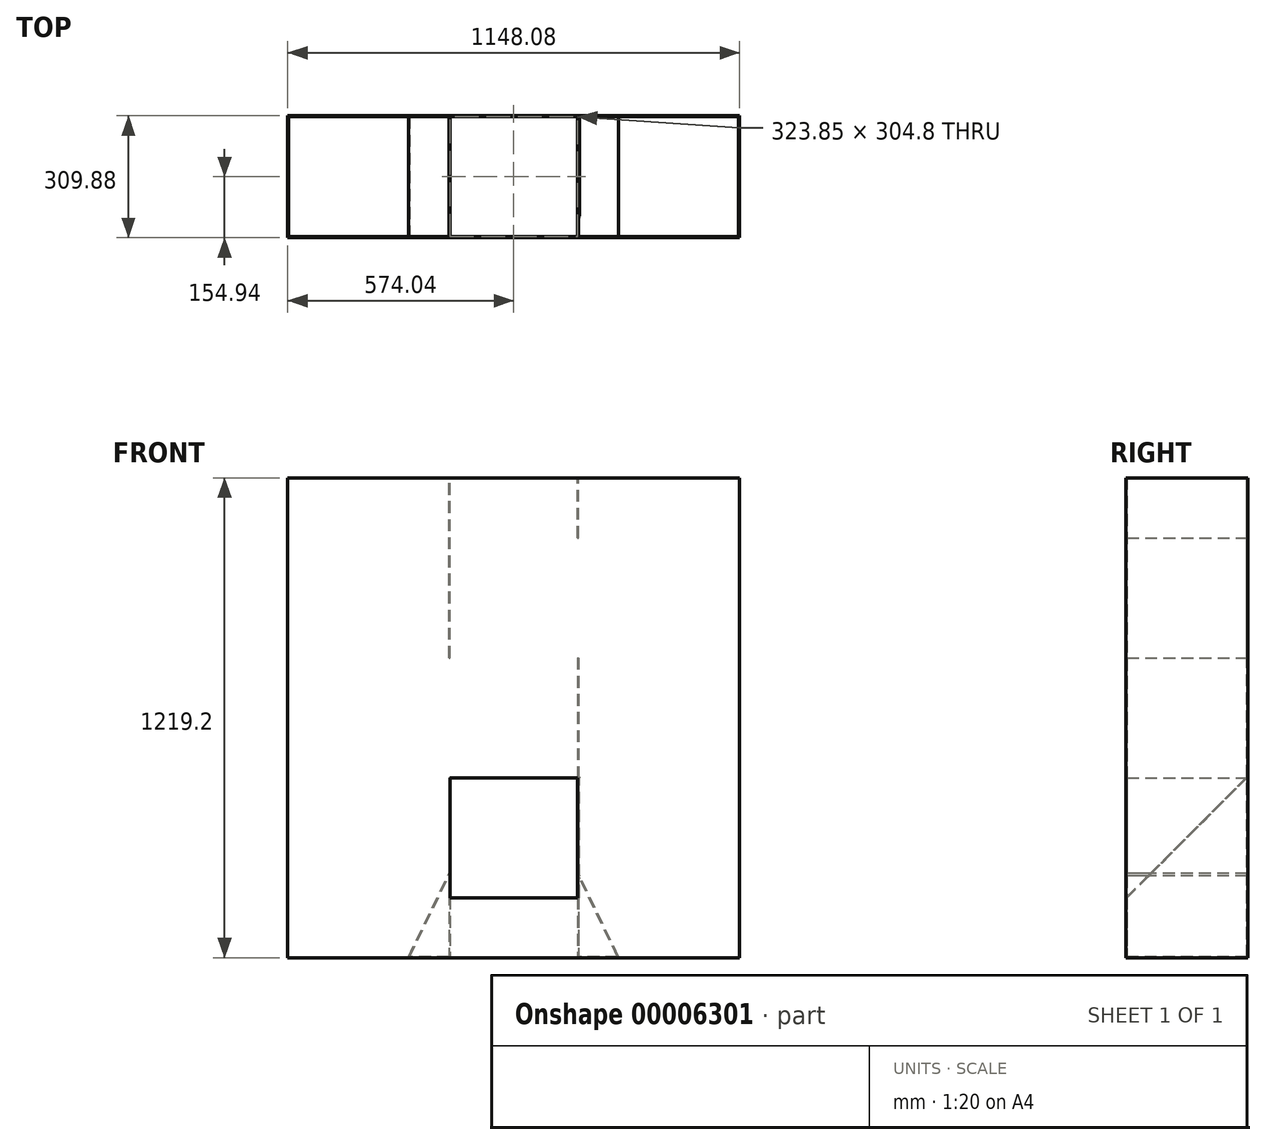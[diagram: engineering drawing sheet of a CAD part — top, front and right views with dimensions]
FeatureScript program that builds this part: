
annotation { "Feature Type Name" : "Feature", "Feature Type Description" : "" }
export const myFeature = defineFeature(function(context is Context, id is Id, definition is map)
    precondition{}
    {
        {
            var Q0;
            Q0=qCreatedBy(makeId("Front.planeOp"),FACE);
            var sketch = newSketch(context, id + "F0", { "sketchPlane" : qUnion([Q0])});
            skLineSegment(sketch, "E0", {"start": v(0, 0) * mm, "end": v(0, 1219.2) * mm});
            skLineSegment(sketch, "E1", {"start": v(0, 1219.2) * mm, "end": v(1148.08, 1219.2) * mm});
            skLineSegment(sketch, "E2", {"start": v(1148.08, 1219.2) * mm, "end": v(1148.08, 0) * mm});
            skLineSegment(sketch, "E3", {"start": v(1148.08, 0) * mm, "end": v(0, 0) * mm});
            skSolve(sketch);
        }
        {
            var Q0;
            Q0=makeQuery(id+"F0.imprint","IMPRINT",FACE,{"disambiguationData":[TD([[makeQuery(id+"F0.imprint","IMPRINT",EDGE,{"derivedFrom":sQuery(id+"F0.wireOp",EDGE,"E0")}),-1.0]])]});
            extrude(context, id + "F1", {"entities" : qUnion([Q0]), "depth" : 309.88 * mm});
        }
        {
            var Q0;
            Q0=makeQuery(id+"F1.opExtrude","SWEPT_FACE",FACE,{"disambiguationData":[OSD([sQuery(id+"F0.wireOp",EDGE,"E1")])]});
            shell(context, id + "F2", {"entities" : qUnion([Q0]), "thickness" : 2.54 * mm});
        }
        {
            var Q0;
            Q0=makeQuery(id+"F1.opExtrude","SWEPT_FACE",FACE,{"disambiguationData":[OSD([sQuery(id+"F0.wireOp",EDGE,"E3")])]});
            var sketch = newSketch(context, id + "F3", { "sketchPlane" : qUnion([Q0])});
            skLineSegment(sketch, "E4.0", {"start": v(0, 309.88) * mm, "end": v(0, 0) * mm});
            skLineSegment(sketch, "E4.1", {"start": v(1148.08, 309.88) * mm, "end": v(0, 309.88) * mm});
            skLineSegment(sketch, "E4.2", {"start": v(1148.08, 309.88) * mm, "end": v(1148.08, 0) * mm});
            skLineSegment(sketch, "E4.3", {"start": v(1148.08, 0) * mm, "end": v(0, 0) * mm});
            skLineSegment(sketch, "E5", {"start": v(0, 154.94) * mm, "end": v(1148.08, 154.94) * mm, "construction": true});
            skLineSegment(sketch, "E6", {"start": v(409.58, 307.34) * mm, "end": v(409.58, 2.54) * mm});
            skLineSegment(sketch, "E7", {"start": v(412.12, 307.34) * mm, "end": v(412.12, 2.54) * mm});
            skLineSegment(sketch, "E8.0", {"start": v(2.54, 307.34) * mm, "end": v(2.54, 2.54) * mm});
            skLineSegment(sketch, "E9", {"start": v(574.04, 307.34) * mm, "end": v(574.04, 0) * mm, "construction": true});
            skLineSegment(sketch, "E10.trimOffspring", {"start": v(574.04, 307.34) * mm, "end": v(2.54, 307.34) * mm});
            skLineSegment(sketch, "E11.trimOffspring", {"start": v(574.04, 2.54) * mm, "end": v(2.54, 2.54) * mm});
            skPoint(sketch, "E12.orphan", {"position": v(574.04, 309.88) * mm});
            skLineSegment(sketch, "E13.0.MirrorCS", {"start": v(735.97, 307.34) * mm, "end": v(735.97, 2.54) * mm});
            skLineSegment(sketch, "E14.0.MirrorCS", {"start": v(738.5, 307.34) * mm, "end": v(738.5, 2.54) * mm});
            skLineSegment(sketch, "E15.0.MirrorCS", {"start": v(1145.54, 307.34) * mm, "end": v(1145.54, 2.54) * mm});
            skLineSegment(sketch, "E16.0.MirrorCS", {"start": v(574.04, 307.34) * mm, "end": v(1145.54, 307.34) * mm});
            skLineSegment(sketch, "E17.0.MirrorCS", {"start": v(574.04, 2.54) * mm, "end": v(1145.54, 2.54) * mm});
            skLineSegment(sketch, "E18", {"start": v(307.34, 307.34) * mm, "end": v(307.34, 2.54) * mm});
            skLineSegment(sketch, "E19.0.MirrorCS", {"start": v(840.74, 307.34) * mm, "end": v(840.74, 2.54) * mm});
            skSolve(sketch);
        }
        {
            var Q0;
            {var subQ2=sQuery(id+"F3.wireOp",EDGE,"E8.0");Q0=makeQuery(id+"F3.imprint","IMPRINT",FACE,{"disambiguationData":[TD([[makeQuery(id+"F3.imprint","IMPRINT",EDGE,{"derivedFrom":subQ2}),1.0]])]});}
            var Q1;
            {var subQ4=sQuery(id+"F3.wireOp",EDGE,"E7");Q1=makeQuery(id+"F3.imprint","IMPRINT",FACE,{"disambiguationData":[TD([[makeQuery(id+"F3.imprint","IMPRINT",EDGE,{"derivedFrom":subQ4}),1.0]])]});}
            var Q2;
            {var subQ2=sQuery(id+"F3.wireOp",EDGE,"E15.0.MirrorCS");Q2=makeQuery(id+"F3.imprint","IMPRINT",FACE,{"disambiguationData":[TD([[makeQuery(id+"F3.imprint","IMPRINT",EDGE,{"derivedFrom":subQ2}),-1.0]])]});}
            var Q3;
            Q3=makeQuery(id+"F2.opShell","OFFSET_FACE",FACE,{"disambiguationData":[OSD([sQuery(id+"F0.wireOp",EDGE,"E3")])]});
            extrude(context, id + "F4", {"entities" : qUnion([Q0, Q1, Q2]), "operationType" : NewBodyOperationType.REMOVE, "endBound" : BoundingType.UP_TO_SURFACE, "oppositeDirection" : true, "endBoundEntityFace" : qUnion([Q3]), "depth" : 25.4 * mm});
        }
        {
            var Q0;
            {var subQ2=sQuery(id+"F3.wireOp",EDGE,"E13.0.MirrorCS");Q0=makeQuery(id+"F3.imprint","IMPRINT",FACE,{"disambiguationData":[TD([[makeQuery(id+"F3.imprint","IMPRINT",EDGE,{"derivedFrom":subQ2}),1.0]])]});}
            extrude(context, id + "F5", {"entities" : qUnion([Q0]), "operationType" : NewBodyOperationType.ADD, "oppositeDirection" : true, "depth" : 762 * mm});
        }
        {
            var Q0;
            {var subQ2=sQuery(id+"F3.wireOp",EDGE,"E6");Q0=makeQuery(id+"F3.imprint","IMPRINT",FACE,{"disambiguationData":[TD([[makeQuery(id+"F3.imprint","IMPRINT",EDGE,{"derivedFrom":subQ2}),1.0]])]});}
            extrude(context, id + "F6", {"entities" : qUnion([Q0]), "operationType" : NewBodyOperationType.ADD, "oppositeDirection" : true, "depth" : 457.2 * mm});
        }
        {
            var Q0;
            Q0=makeQuery(id+"F1.opExtrude","SWEPT_FACE",FACE,{"disambiguationData":[OSD([sQuery(id+"F0.wireOp",EDGE,"E1")])]});
            var sketch = newSketch(context, id + "F7", { "sketchPlane" : qUnion([Q0])});
            skLineSegment(sketch, "E20.0", {"start": v(735.97, -307.34) * mm, "end": v(735.97, -2.54) * mm});
            skLineSegment(sketch, "E21.0", {"start": v(738.5, -307.34) * mm, "end": v(738.5, -2.54) * mm});
            skLineSegment(sketch, "E22.0", {"start": v(2.54, -307.34) * mm, "end": v(1145.54, -307.34) * mm});
            skLineSegment(sketch, "E23.0", {"start": v(412.12, -307.34) * mm, "end": v(412.12, -2.54) * mm});
            skLineSegment(sketch, "E24.0", {"start": v(409.58, -307.34) * mm, "end": v(409.58, -2.54) * mm});
            skLineSegment(sketch, "E25.0", {"start": v(2.54, -2.54) * mm, "end": v(1145.54, -2.54) * mm});
            skSolve(sketch);
        }
        {
            var Q0;
            Q0=makeQuery(id+"F1.opExtrude","CAP_FACE",FACE,{"disambiguationData":[OSD([sQuery(id+"F0.wireOp",EDGE,"E0"),sQuery(id+"F0.wireOp",EDGE,"E1"),sQuery(id+"F0.wireOp",EDGE,"E2"),sQuery(id+"F0.wireOp",EDGE,"E3")])],"isStart":false});
            var sketch = newSketch(context, id + "F8", { "sketchPlane" : qUnion([Q0])});
            skLineSegment(sketch, "E26", {"start": v(574.04, 0) * mm, "end": v(574.04, 1219.2) * mm, "construction": true});
            skLineSegment(sketch, "E27.0", {"start": v(409.58, 1219.2) * mm, "end": v(409.58, 2.54) * mm});
            skLineSegment(sketch, "E28.0", {"start": v(409.58, 2.54) * mm, "end": v(307.34, 2.54) * mm});
            skLineSegment(sketch, "E29", {"start": v(307.34, 2.54) * mm, "end": v(409.58, 214.23) * mm});
            skLineSegment(sketch, "E30", {"start": v(310.16, 2.54) * mm, "end": v(409.58, 208.4) * mm});
            skLineSegment(sketch, "E31.0.MirrorCS", {"start": v(837.92, 2.54) * mm, "end": v(738.5, 208.4) * mm});
            skLineSegment(sketch, "E32.0.MirrorCS", {"start": v(840.74, 2.54) * mm, "end": v(738.5, 214.23) * mm});
            skLineSegment(sketch, "E33.0.MirrorCS", {"start": v(738.5, 2.54) * mm, "end": v(840.74, 2.54) * mm});
            skLineSegment(sketch, "E34.0", {"start": v(412.12, 1219.2) * mm, "end": v(412.12, 0) * mm});
            skLineSegment(sketch, "E35.0", {"start": v(0, 1219.2) * mm, "end": v(1148.08, 1219.2) * mm});
            skLineSegment(sketch, "E36.0.MirrorCS", {"start": v(738.5, 1219.2) * mm, "end": v(738.5, 2.54) * mm});
            skLineSegment(sketch, "E37.0.MirrorCS", {"start": v(735.97, 1219.2) * mm, "end": v(735.97, 0) * mm});
            skLineSegment(sketch, "E38", {"start": v(412.12, 152.4) * mm, "end": v(738.5, 152.4) * mm});
            skLineSegment(sketch, "E39", {"start": v(735.97, 457.2) * mm, "end": v(409.58, 457.2) * mm});
            skSolve(sketch);
        }
        {
            var Q0;
            {var subQ1=sQuery(id+"F8.wireOp",EDGE,"E29");Q0=makeQuery(id+"F8.imprint","IMPRINT",FACE,{"disambiguationData":[TD([[makeQuery(id+"F8.imprint","IMPRINT",EDGE,{"derivedFrom":subQ1}),-1.0]])]});}
            var Q1;
            {var subQ2=sQuery(id+"F8.wireOp",EDGE,"E31.0.MirrorCS");Q1=makeQuery(id+"F8.imprint","IMPRINT",FACE,{"disambiguationData":[TD([[makeQuery(id+"F8.imprint","IMPRINT",EDGE,{"derivedFrom":subQ2}),-1.0]])]});}
            var Q2;
            Q2=sQuery(id+"F8.wireOp",EDGE,"E29");
            var Q3;
            Q3=sQuery(id+"F8.wireOp",EDGE,"E30");
            var Q4;
            Q4=makeQuery(id+"F1.opExtrude","CAP_FACE",FACE,{"disambiguationData":[OSD([sQuery(id+"F0.wireOp",EDGE,"E0"),sQuery(id+"F0.wireOp",EDGE,"E1"),sQuery(id+"F0.wireOp",EDGE,"E2"),sQuery(id+"F0.wireOp",EDGE,"E3")])],"isStart":true});
            extrude(context, id + "F9", {"entities" : qUnion([Q0, Q1]), "operationType" : NewBodyOperationType.ADD, "surfaceEntities" : qUnion([Q2, Q3]), "endBound" : BoundingType.UP_TO_SURFACE, "oppositeDirection" : true, "endBoundEntityFace" : qUnion([Q4]), "depth" : 25.4 * mm});
        }
        {
            var Q0;
            {var subQ1=sQuery(id+"F8.wireOp",EDGE,"E34.0");var subQ5=sQuery(id+"F8.wireOp",EDGE,"E38");var subQ7=makeQuery(id+"F8.imprint","INTERSECT",VERTEX,{"derivedFrom":[subQ1,subQ5]});Q0=makeQuery(id+"F8.imprint","IMPRINT",FACE,{"disambiguationData":[TD([[makeQuery(id+"F8.imprint","IMPRINT",EDGE,{"disambiguationData":[TD([[subQ7,1.0]])],"derivedFrom":subQ1}),1.0]])]});}
            var Q1;
            {var subQ0=sQuery(id+"F0.wireOp",EDGE,"E0");var subQ1=sQuery(id+"F0.wireOp",EDGE,"E1");var subQ2=sQuery(id+"F0.wireOp",EDGE,"E2");var subQ3=sQuery(id+"F0.wireOp",EDGE,"E3");var subQ4=sQuery(id+"F3.wireOp",EDGE,"E10.trimOffspring");var subQ5=sQuery(id+"F3.wireOp",EDGE,"E16.0.MirrorCS");var subQ6=makeQuery(id+"F4.boolean.opBoolean","MERGE",FACE,{"derivedFrom":[makeQuery(id+"F2.opShell","OFFSET_FACE",FACE,{"disambiguationData":[OSD([subQ0,subQ1,subQ2,subQ3]),TDD([makeQuery(id+"F1.opExtrude","CAP_FACE",FACE,{"disambiguationData":[OSD([subQ0,subQ1,subQ2,subQ3])],"isStart":false})])]}),makeQuery(id+"F4.opExtrude","SWEPT_FACE",FACE,{"disambiguationData":[OSD([subQ4,subQ5])]}),makeQuery(id+"F4.opExtrude","SWEPT_FACE",FACE,{"disambiguationData":[OSD([subQ4])]}),makeQuery(id+"F4.opExtrude","SWEPT_FACE",FACE,{"disambiguationData":[OSD([subQ5])]})]});Q1=qUnion([makeQuery(id+"F9.boolean.opBoolean","SPLIT",FACE,{"disambiguationData":[TD([makeQuery(id+"F9.opExtrude","SWEPT_FACE",FACE,{"disambiguationData":[OSD([sQuery(id+"F8.wireOp",EDGE,"E30")])]})])],"derivedFrom":subQ6}),makeQuery(id+"F9.boolean.opBoolean","SPLIT",FACE,{"disambiguationData":[TD([makeQuery(id+"F1.opExtrude","SWEPT_FACE",FACE,{"disambiguationData":[OSD([subQ1])]})])],"derivedFrom":subQ6}),makeQuery(id+"F9.boolean.opBoolean","SPLIT",FACE,{"disambiguationData":[TD([makeQuery(id+"F9.opExtrude","SWEPT_FACE",FACE,{"disambiguationData":[OSD([sQuery(id+"F8.wireOp",EDGE,"E31.0.MirrorCS")])]})])],"derivedFrom":subQ6})]);}
            extrude(context, id + "F10", {"entities" : qUnion([Q0]), "operationType" : NewBodyOperationType.REMOVE, "endBound" : BoundingType.UP_TO_SURFACE, "oppositeDirection" : true, "endBoundEntityFace" : qUnion([Q1]), "depth" : 25.4 * mm});
        }
        {
            var Q0;
            {var subQ0=sQuery(id+"F3.wireOp",EDGE,"E14.0.MirrorCS");Q0=makeQuery(id+"F9.boolean.opBoolean","SPLIT",FACE,{"disambiguationData":[TD([makeQuery(id+"F9.opExtrude","SWEPT_FACE",FACE,{"disambiguationData":[OSD([sQuery(id+"F8.wireOp",EDGE,"E32.0.MirrorCS")])]})])],"derivedFrom":makeQuery(id+"F5.opExtrude","SWEPT_FACE",FACE,{"disambiguationData":[OSD([subQ0])]})});}
            var sketch = newSketch(context, id + "F11", { "sketchPlane" : qUnion([Q0])});
            skLineSegment(sketch, "E40.0", {"start": v(-307.34, 152.4) * mm, "end": v(-309.88, 152.4) * mm});
            skLineSegment(sketch, "E41", {"start": v(-307.34, 152.4) * mm, "end": v(-2.54, 457.2) * mm});
            skLineSegment(sketch, "E42.0", {"start": v(-2.54, 762) * mm, "end": v(-2.54, 214.23) * mm});
            skLineSegment(sketch, "E43", {"start": v(-309.88, 152.4) * mm, "end": v(-2.54, 459.74) * mm});
            skSolve(sketch);
        }
        {
            var Q0;
            {var subQ3=sQuery(id+"F11.wireOp",EDGE,"E41");var subQ6=sQuery(id+"F11.wireOp",EDGE,"E40.0");var subQ7=sQuery(id+"F11.wireOp",EDGE,"E42.0");var subQ9=makeQuery(id+"F11.imprint","INTERSECT",VERTEX,{"derivedFrom":[subQ3,subQ7]});Q0=qUnion([makeQuery(id+"F11.imprint","IMPRINT",FACE,{"disambiguationData":[TD([[makeQuery(id+"F11.imprint","IMPRINT",EDGE,{"derivedFrom":subQ6}),-1.0]])]}),makeQuery(id+"F11.imprint","IMPRINT",FACE,{"disambiguationData":[TD([[makeQuery(id+"F11.imprint","IMPRINT",EDGE,{"disambiguationData":[TD([[subQ9,1.0]])],"derivedFrom":subQ7}),-1.0]])]})]);}
            extrude(context, id + "F12", {"entities" : qUnion([Q0]), "operationType" : NewBodyOperationType.ADD, "depth" : 3.17 * mm});
        }
        {
            var Q0;
            {var subQ2=sQuery(id+"F7.wireOp",EDGE,"E23.0");Q0=makeQuery(id+"F7.imprint","IMPRINT",FACE,{"disambiguationData":[TD([[makeQuery(id+"F7.imprint","IMPRINT",EDGE,{"derivedFrom":subQ2}),1.0]])]});}
            extrude(context, id + "F13", {"entities" : qUnion([Q0]), "operationType" : NewBodyOperationType.ADD, "oppositeDirection" : true, "depth" : 457.2 * mm});
        }
        {
            var Q0;
            {var subQ2=sQuery(id+"F7.wireOp",EDGE,"E20.0");Q0=makeQuery(id+"F7.imprint","IMPRINT",FACE,{"disambiguationData":[TD([[makeQuery(id+"F7.imprint","IMPRINT",EDGE,{"derivedFrom":subQ2}),-1.0]])]});}
            extrude(context, id + "F14", {"entities" : qUnion([Q0]), "operationType" : NewBodyOperationType.ADD, "oppositeDirection" : true, "depth" : 152.4 * mm});
        }
    });
